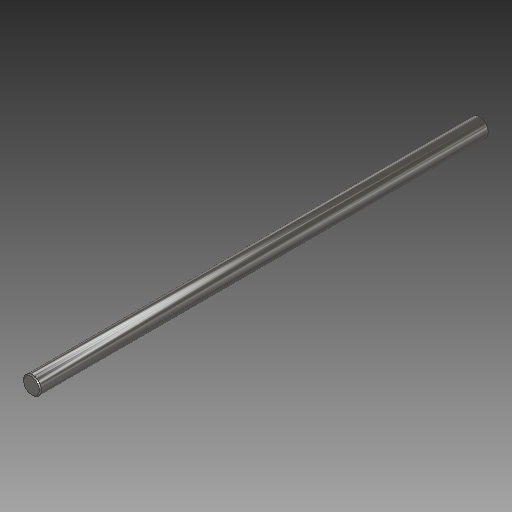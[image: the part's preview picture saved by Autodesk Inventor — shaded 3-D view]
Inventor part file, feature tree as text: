
AUTODESK INVENTOR PART (.ipt)
format: ipt  version: 2019 (Build 230136000, 136)  size: 102,400 bytes
history: native  units: mm
features: extrude x1, chamfer x1, sketch x1
ambient origin geometry x8: Origin, YZ Plane, XZ Plane, XY Plane, X Axis, Y Axis, Z Axis, Center Point
bodies: Solid1 (feature_tree)
feature tree (3):
  extrude  "Extrusion1"  Depth=200.0mm TaperAngle=0.0deg
  chamfer  "Chamfer1"  Distance=0.5mm Angle=45.0deg
  sketch  "Sketch1"  dims[d0=8.0mm d1=200.0mm d2=0.0mm d3=0.5mm d4=2.0mm d5=45.0deg]
